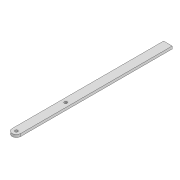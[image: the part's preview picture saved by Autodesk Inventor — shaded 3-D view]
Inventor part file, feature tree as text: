
AUTODESK INVENTOR PART (.ipt)
format: ipt  version: 2022 (Build 260153000, 153)  size: 99,840 bytes
history: native  units: mm
features: extrude x2, sketch x2
ambient origin geometry x8: Origin, YZ Plane, XZ Plane, XY Plane, X Axis, Y Axis, Z Axis, Center Point
bodies: Solid1 (feature_tree)
feature tree (4):
  extrude  "Extrusion1"  Depth=3.3mm
  extrude  "Extrusion2"  Depth=355.998mm
  sketch  "Sketch1"  dims[d0=3.3mm d1=3.3mm]
  sketch  "Sketch2"  dims[d2=10.0mm d3=355.998mm d6=3.0mm d7=0.0mm d14=3.3mm d15=57.376mm d16=10.0mm d17=0.0mm]
